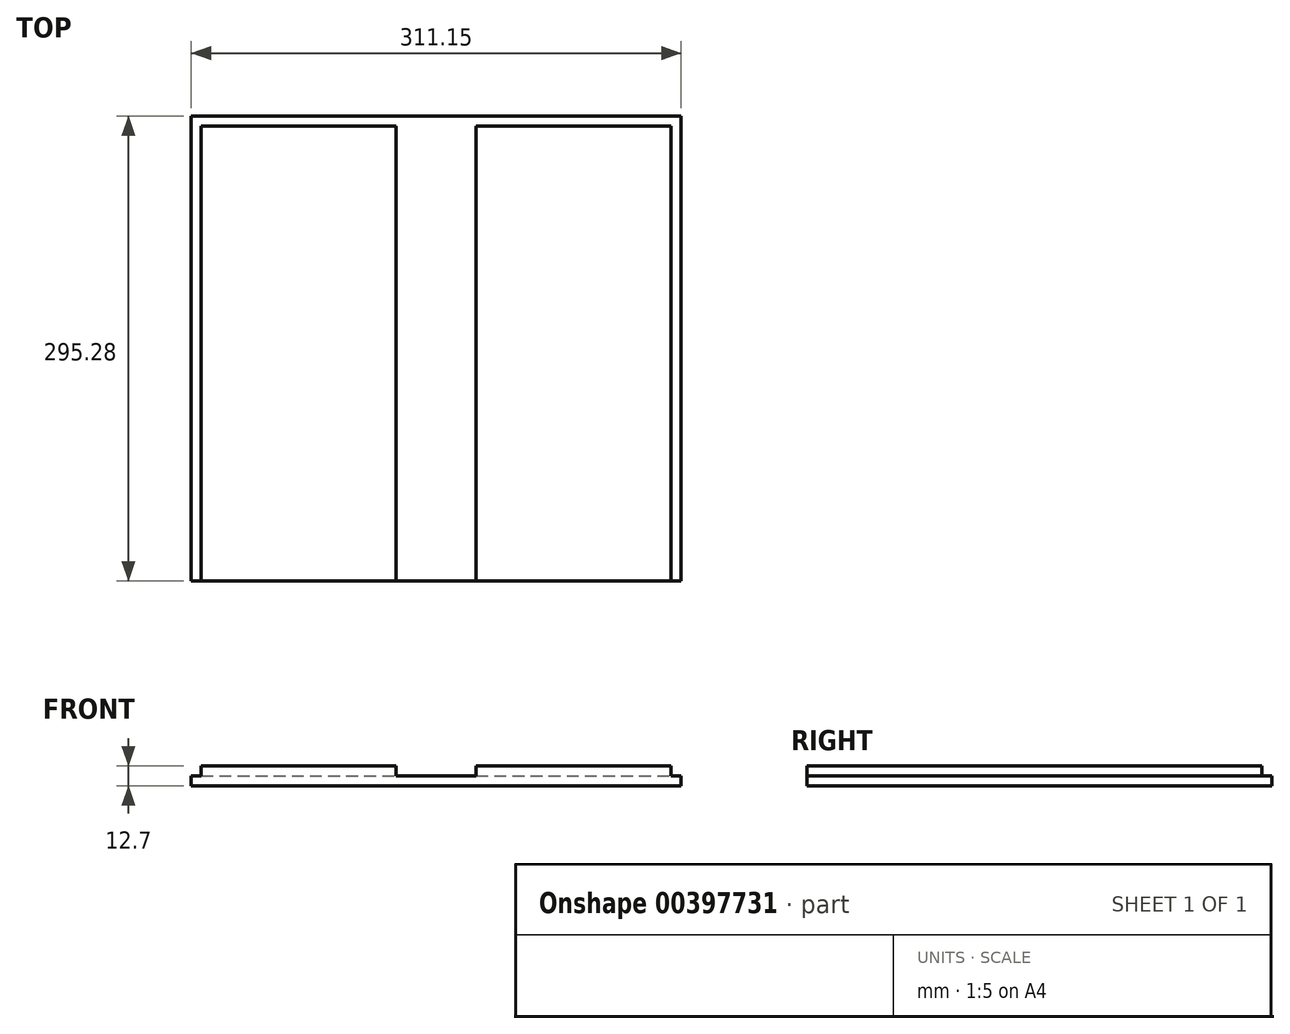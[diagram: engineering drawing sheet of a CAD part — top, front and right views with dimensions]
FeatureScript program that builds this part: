
annotation { "Feature Type Name" : "Feature", "Feature Type Description" : "" }
export const myFeature = defineFeature(function(context is Context, id is Id, definition is map)
    precondition{}
    {
        {
            var Q0;
            Q0=qCreatedBy(makeId("Top.planeOp"),FACE);
            var sketch = newSketch(context, id + "F0", { "sketchPlane" : qUnion([Q0])});
            skLineSegment(sketch, "E0.bottom", {"start": v(0, 0) * mm, "end": v(311.15, 0) * mm});
            skLineSegment(sketch, "E0.top", {"start": v(0, 295.28) * mm, "end": v(311.15, 295.28) * mm});
            skLineSegment(sketch, "E0.left", {"start": v(0, 0) * mm, "end": v(0, 295.28) * mm});
            skLineSegment(sketch, "E0.right", {"start": v(311.15, 0) * mm, "end": v(311.15, 295.28) * mm});
            skLineSegment(sketch, "E1.bottom", {"start": v(6.35, 288.93) * mm, "end": v(304.8, 288.93) * mm});
            skLineSegment(sketch, "E1.left", {"start": v(6.35, 288.93) * mm, "end": v(6.35, 0) * mm});
            skLineSegment(sketch, "E1.right", {"start": v(304.8, 288.93) * mm, "end": v(304.8, 0) * mm});
            skSolve(sketch);
        }
        {
            var Q0;
            Q0=makeQuery(id+"F0.imprint","IMPRINT",FACE,{"disambiguationData":[TD([[makeQuery(id+"F0.imprint","IMPRINT",EDGE,{"derivedFrom":sQuery(id+"F0.wireOp",EDGE,"E0.top")}),-1.0]])]});
            extrude(context, id + "F1", {"entities" : qUnion([Q0]), "depth" : 6.35 * mm});
        }
        {
            var Q0;
            Q0=makeQuery(id+"F0.imprint","IMPRINT",FACE,{"disambiguationData":[TD([[makeQuery(id+"F0.imprint","IMPRINT",EDGE,{"derivedFrom":sQuery(id+"F0.wireOp",EDGE,"E1.bottom")}),-1.0]])]});
            extrude(context, id + "F2", {"entities" : qUnion([Q0]), "operationType" : NewBodyOperationType.ADD, "depth" : 12.7 * mm});
        }
        {
            var Q0;
            {var subQ0=sQuery(id+"F0.wireOp",EDGE,"E0.bottom");Q0=makeQuery(id+"F2.boolean.opBoolean","MERGE",FACE,{"derivedFrom":[makeQuery(id+"F1.opExtrude","SWEPT_FACE",FACE,{"disambiguationData":[OSD([subQ0]),TDD([makeQuery(id+"F0.imprint","IMPRINT",EDGE,{"disambiguationData":[TD([[makeQuery(id+"F0.imprint","INTERSECT",VERTEX,{"derivedFrom":[subQ0,sQuery(id+"F0.wireOp",EDGE,"E0.left")]}),-1.0]])],"derivedFrom":subQ0})])]}),makeQuery(id+"F1.opExtrude","SWEPT_FACE",FACE,{"disambiguationData":[OSD([subQ0]),TDD([makeQuery(id+"F0.imprint","IMPRINT",EDGE,{"disambiguationData":[TD([[makeQuery(id+"F0.imprint","INTERSECT",VERTEX,{"derivedFrom":[subQ0,sQuery(id+"F0.wireOp",EDGE,"E0.right")]}),1.0]])],"derivedFrom":subQ0})])]}),makeQuery(id+"F2.opExtrude","SWEPT_FACE",FACE,{"disambiguationData":[OSD([subQ0])]})]});}
            var sketch = newSketch(context, id + "F3", { "sketchPlane" : qUnion([Q0])});
            skLineSegment(sketch, "E2.bottom", {"start": v(130.17, 12.7) * mm, "end": v(180.97, 12.7) * mm});
            skLineSegment(sketch, "E2.top", {"start": v(130.17, 6.35) * mm, "end": v(180.97, 6.35) * mm});
            skLineSegment(sketch, "E2.left", {"start": v(130.17, 12.7) * mm, "end": v(130.17, 6.35) * mm});
            skLineSegment(sketch, "E2.right", {"start": v(180.97, 12.7) * mm, "end": v(180.97, 6.35) * mm});
            skSolve(sketch);
        }
        {
            var Q0;
            Q0=makeQuery(id+"F3.imprint","IMPRINT",FACE,{"disambiguationData":[TD([[makeQuery(id+"F3.imprint","IMPRINT",EDGE,{"derivedFrom":sQuery(id+"F3.wireOp",EDGE,"E2.bottom")}),-1.0]])]});
            extrude(context, id + "F4", {"entities" : qUnion([Q0]), "operationType" : NewBodyOperationType.REMOVE, "endBound" : BoundingType.THROUGH_ALL, "oppositeDirection" : true, "depth" : 25.4 * mm});
        }
    });
